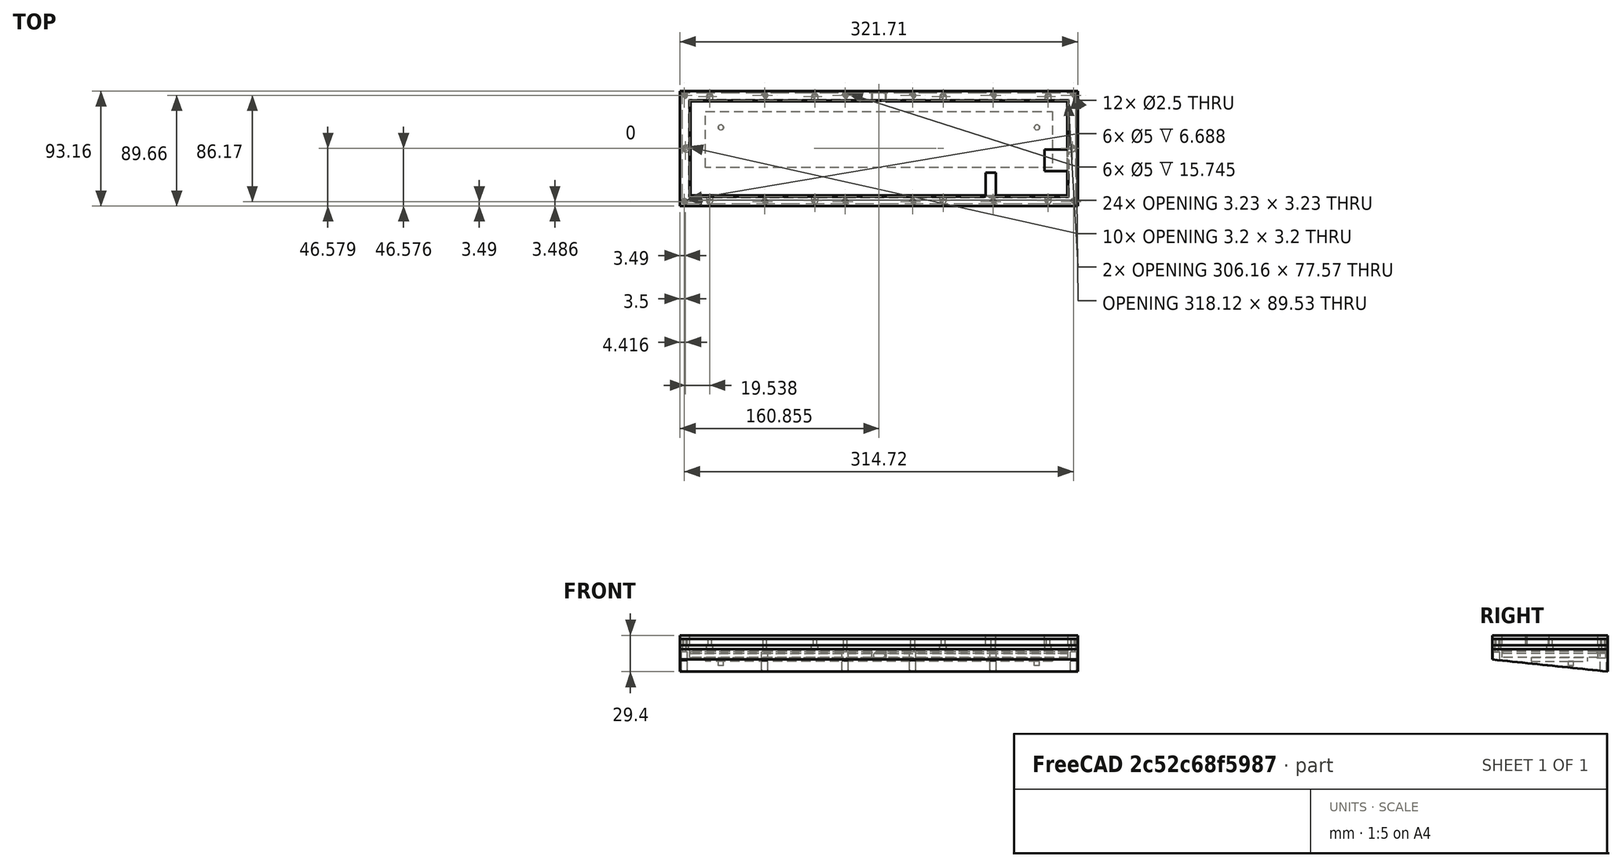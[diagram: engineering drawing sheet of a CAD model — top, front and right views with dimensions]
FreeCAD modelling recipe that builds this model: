
FCSTD DOCUMENT  (FreeCAD 0.19R24267 +99 (Git))
Label: chasma-case
License: All rights reserved
LicenseURL: http://en.wikipedia.org/wiki/All_rights_reserved
objects: Part::Feature×50, Part::MultiFuse×27, Part::Cylinder×24, Part::Extrusion×10, Part::Cut×4, Part::Compound×1
note: 116 computed .brp shape members not serialized (recipe doc carries the construction recipe); baked Part::Feature solids carry a one-line shape summary decoded from their .brp

FEATURE [Part::Feature] path7555
  shape: bbox 321.7 x 93.16 x 2e-07 mm, 0 faces, 0 solids (baked)
FEATURE [Part::Extrusion] Extrude
  Base = -> path7555
  Dir = (0,0,-1)
  DirMode = 0
  FaceMakerClass = Part::FaceMakerBullseye
  LengthFwd = 100
  LengthRev = 0
  Solid = true
  Symmetric = false
FEATURE [Part::Feature] path7555001
  Placement = pos=(-75,25,-14.03) rot=(-1,0,0;0.10472rad)
  shape: bbox 482.6 x 139 x 14.61 mm, 0 faces, 0 solids (baked)
FEATURE [Part::Extrusion] Extrude001
  Base = -> path7555001
  Dir = (0,-0.104528,-0.994522)
  DirMode = 2
  FaceMakerClass = Part::FaceMakerBullseye
  LengthFwd = 100
  LengthRev = 0
  Solid = true
  Symmetric = false
FEATURE [Part::Cut] Cut  label="bottom"
  Base = -> Extrude
  Tool = -> Extrude001
FEATURE [Part::Feature] path6345_8_6_9_7_6_0_4
  shape: bbox 306.2 x 77.57 x 2e-07 mm, 0 faces, 0 solids (baked)
FEATURE [Part::Feature] path6345_8_6_9_7_6_0_4001
  shape: bbox 321.7 x 93.16 x 2e-07 mm, 0 faces, 0 solids (baked)
FEATURE [Part::MultiFuse] Fusion
  Shapes = -> [path6345_8_6_9_7_6_0_4001,path6345_8_6_9_7_6_0_4]
FEATURE [Part::Extrusion] Extrude002  label="bottom-middle"
  Base = -> Fusion
  Dir = (0,0,1)
  DirMode = 2
  FaceMakerClass = Part::FaceMakerBullseye
  LengthFwd = 6.6
  LengthRev = 0
  Solid = true
  Symmetric = false
FEATURE [Part::MultiFuse] Fusion004  label="bottom-base"
  Shapes = -> [Cut,Extrude002]
FEATURE [Part::Cylinder] Cylinder  label="円柱"
  Angle = 360
  AttacherType = Attacher::AttachEngine3D
  Height = 30
  Placement = pos=(0,0,-18.6) rot=(0,0,1;0rad)
  Radius = 1.25
FEATURE [Part::Cylinder] Cylinder002  label="円柱001"
  Angle = 360
  AttacherType = Attacher::AttachEngine3D
  Height = 25
  Placement = pos=(0,0,-20.6) rot=(0,0,1;0rad)
  Radius = 2.5
FEATURE [Part::MultiFuse] Fusion006
  Placement = pos=(3.55,-3.55,0) rot=(0,0,1;0rad)
  Shapes = -> [Cylinder002,Cylinder]
FEATURE [Part::Cylinder] Cylinder003  label="円柱002"
  Angle = 360
  AttacherType = Attacher::AttachEngine3D
  Height = 25
  Placement = pos=(0,0,-20.6) rot=(0,0,1;0rad)
  Radius = 2.5
FEATURE [Part::Cylinder] Cylinder004  label="円柱003"
  Angle = 360
  AttacherType = Attacher::AttachEngine3D
  Height = 30
  Placement = pos=(0,0,-18.6) rot=(0,0,1;0rad)
  Radius = 1.25
FEATURE [Part::MultiFuse] Fusion007
  Placement = pos=(3.55,-89.72,0) rot=(0,0,1;0rad)
  Shapes = -> [Cylinder003,Cylinder004]
FEATURE [Part::MultiFuse] Fusion008
  Shapes = -> [Fusion006,Fusion007]
FEATURE [Part::Cylinder] Cylinder005  label="円柱004"
  Angle = 360
  AttacherType = Attacher::AttachEngine3D
  Height = 25
  Placement = pos=(0,0,-20.6) rot=(0,0,1;0rad)
  Radius = 2.5
FEATURE [Part::Cylinder] Cylinder006  label="円柱005"
  Angle = 360
  AttacherType = Attacher::AttachEngine3D
  Height = 25
  Placement = pos=(0,0,-20.6) rot=(0,0,1;0rad)
  Radius = 2.5
FEATURE [Part::Cylinder] Cylinder007  label="円柱006"
  Angle = 360
  AttacherType = Attacher::AttachEngine3D
  Height = 30
  Placement = pos=(0,0,-18.6) rot=(0,0,1;0rad)
  Radius = 1.25
FEATURE [Part::Cylinder] Cylinder008  label="円柱007"
  Angle = 360
  AttacherType = Attacher::AttachEngine3D
  Height = 30
  Placement = pos=(0,0,-18.6) rot=(0,0,1;0rad)
  Radius = 1.25
FEATURE [Part::MultiFuse] Fusion009
  Placement = pos=(3.55,-89.72,0) rot=(0,0,1;0rad)
  Shapes = -> [Cylinder006,Cylinder007]
FEATURE [Part::MultiFuse] Fusion011
  Placement = pos=(3.55,-3.55,0) rot=(0,0,1;0rad)
  Shapes = -> [Cylinder005,Cylinder008]
FEATURE [Part::MultiFuse] Fusion010
  Placement = pos=(130,0,0) rot=(0,0,1;0rad)
  Shapes = -> [Fusion011,Fusion009]
FEATURE [Part::Cylinder] Cylinder009  label="円柱008"
  Angle = 360
  AttacherType = Attacher::AttachEngine3D
  Height = 30
  Placement = pos=(0,0,-18.6) rot=(0,0,1;0rad)
  Radius = 1.25
FEATURE [Part::Cylinder] Cylinder010  label="円柱009"
  Angle = 360
  AttacherType = Attacher::AttachEngine3D
  Height = 25
  Placement = pos=(0,0,-20.6) rot=(0,0,1;0rad)
  Radius = 2.5
FEATURE [Part::Cylinder] Cylinder011  label="円柱010"
  Angle = 360
  AttacherType = Attacher::AttachEngine3D
  Height = 25
  Placement = pos=(0,0,-20.6) rot=(0,0,1;0rad)
  Radius = 2.5
FEATURE [Part::Cylinder] Cylinder012  label="円柱011"
  Angle = 360
  AttacherType = Attacher::AttachEngine3D
  Height = 30
  Placement = pos=(0,0,-18.6) rot=(0,0,1;0rad)
  Radius = 1.25
FEATURE [Part::MultiFuse] Fusion012
  Placement = pos=(3.55,-3.55,0) rot=(0,0,1;0rad)
  Shapes = -> [Cylinder010,Cylinder012]
FEATURE [Part::MultiFuse] Fusion013
  Placement = pos=(3.55,-89.72,0) rot=(0,0,1;0rad)
  Shapes = -> [Cylinder011,Cylinder009]
FEATURE [Part::MultiFuse] Fusion014
  Placement = pos=(65,0,0) rot=(0,0,1;0rad)
  Shapes = -> [Fusion012,Fusion013]
FEATURE [Part::Cylinder] Cylinder013  label="円柱012"
  Angle = 360
  AttacherType = Attacher::AttachEngine3D
  Height = 30
  Placement = pos=(0,0,-18.6) rot=(0,0,1;0rad)
  Radius = 1.25
FEATURE [Part::Cylinder] Cylinder014  label="円柱013"
  Angle = 360
  AttacherType = Attacher::AttachEngine3D
  Height = 30
  Placement = pos=(0,0,-18.6) rot=(0,0,1;0rad)
  Radius = 1.25
FEATURE [Part::Cylinder] Cylinder015  label="円柱014"
  Angle = 360
  AttacherType = Attacher::AttachEngine3D
  Height = 25
  Placement = pos=(0,0,-20.6) rot=(0,0,1;0rad)
  Radius = 2.5
FEATURE [Part::Cylinder] Cylinder016  label="円柱015"
  Angle = 360
  AttacherType = Attacher::AttachEngine3D
  Height = 25
  Placement = pos=(0,0,-20.6) rot=(0,0,1;0rad)
  Radius = 2.5
FEATURE [Part::MultiFuse] Fusion015
  Placement = pos=(3.55,-3.55,0) rot=(0,0,1;0rad)
  Shapes = -> [Cylinder015,Cylinder014]
FEATURE [Part::MultiFuse] Fusion016
  Placement = pos=(3.55,-89.72,0) rot=(0,0,1;0rad)
  Shapes = -> [Cylinder016,Cylinder013]
FEATURE [Part::MultiFuse] Fusion017
  Placement = pos=(184.72,0,0) rot=(0,0,1;0rad)
  Shapes = -> [Fusion015,Fusion016]
FEATURE [Part::Cylinder] Cylinder017  label="円柱016"
  Angle = 360
  AttacherType = Attacher::AttachEngine3D
  Height = 30
  Placement = pos=(0,0,-18.6) rot=(0,0,1;0rad)
  Radius = 1.25
FEATURE [Part::Cylinder] Cylinder018  label="円柱017"
  Angle = 360
  AttacherType = Attacher::AttachEngine3D
  Height = 30
  Placement = pos=(0,0,-18.6) rot=(0,0,1;0rad)
  Radius = 1.25
FEATURE [Part::Cylinder] Cylinder019  label="円柱018"
  Angle = 360
  AttacherType = Attacher::AttachEngine3D
  Height = 25
  Placement = pos=(0,0,-20.6) rot=(0,0,1;0rad)
  Radius = 2.5
FEATURE [Part::Cylinder] Cylinder020  label="円柱019"
  Angle = 360
  AttacherType = Attacher::AttachEngine3D
  Height = 25
  Placement = pos=(0,0,-20.6) rot=(0,0,1;0rad)
  Radius = 2.5
FEATURE [Part::MultiFuse] Fusion018
  Placement = pos=(3.55,-89.72,0) rot=(0,0,1;0rad)
  Shapes = -> [Cylinder020,Cylinder017]
FEATURE [Part::MultiFuse] Fusion019
  Placement = pos=(3.55,-3.55,0) rot=(0,0,1;0rad)
  Shapes = -> [Cylinder019,Cylinder018]
FEATURE [Part::MultiFuse] Fusion020
  Placement = pos=(249.72,0,0) rot=(0,0,1;0rad)
  Shapes = -> [Fusion019,Fusion018]
FEATURE [Part::Cylinder] Cylinder021  label="円柱020"
  Angle = 360
  AttacherType = Attacher::AttachEngine3D
  Height = 25
  Placement = pos=(0,0,-20.6) rot=(0,0,1;0rad)
  Radius = 2.5
FEATURE [Part::Cylinder] Cylinder022  label="円柱021"
  Angle = 360
  AttacherType = Attacher::AttachEngine3D
  Height = 30
  Placement = pos=(0,0,-18.6) rot=(0,0,1;0rad)
  Radius = 1.25
FEATURE [Part::Cylinder] Cylinder023  label="円柱022"
  Angle = 360
  AttacherType = Attacher::AttachEngine3D
  Height = 30
  Placement = pos=(0,0,-18.6) rot=(0,0,1;0rad)
  Radius = 1.25
FEATURE [Part::Cylinder] Cylinder024  label="円柱023"
  Angle = 360
  AttacherType = Attacher::AttachEngine3D
  Height = 25
  Placement = pos=(0,0,-20.6) rot=(0,0,1;0rad)
  Radius = 2.5
FEATURE [Part::MultiFuse] Fusion021
  Placement = pos=(3.55,-3.55,0) rot=(0,0,1;0rad)
  Shapes = -> [Cylinder024,Cylinder023]
FEATURE [Part::MultiFuse] Fusion022
  Placement = pos=(3.55,-89.72,0) rot=(0,0,1;0rad)
  Shapes = -> [Cylinder021,Cylinder022]
FEATURE [Part::MultiFuse] Fusion023
  Placement = pos=(314.72,0,0) rot=(0,0,1;0rad)
  Shapes = -> [Fusion021,Fusion022]
FEATURE [Part::MultiFuse] Fusion024
  Shapes = -> [Fusion008,Fusion010,Fusion014,Fusion017,Fusion020,Fusion023]
FEATURE [Part::Cut] Cut001  label="bottom-screw"
  Base = -> Fusion004
  Tool = -> Fusion024
FEATURE [Part::Feature] path10122_7
  shape: bbox 304.8 x 83.09 x 2e-07 mm, 1 faces, 0 solids (baked)
FEATURE [Part::Extrusion] Extrude006  label="pcb"
  Base = -> path10122_7
  Dir = (0,0,1)
  DirMode = 0
  FaceMakerClass = Part::FaceMakerBullseye
  LengthFwd = 1.6
  LengthRev = 0
  Placement = pos=(0,0,3.4) rot=(0,0,1;0rad)
  Solid = false
  Symmetric = false
FEATURE [Part::Feature] rect340
  shape: bbox 11.23 x 6.92 x 2e-07 mm, 0 faces, 0 solids (baked)
FEATURE [Part::Extrusion] Extrude007  label="usb-box"
  Base = -> rect340
  Dir = (0,0,1)
  DirMode = 0
  FaceMakerClass = Part::FaceMakerBullseye
  LengthFwd = 10
  LengthRev = 0
  Placement = pos=(0,0,-0.5) rot=(0,0,1;0rad)
  Solid = true
  Symmetric = false
FEATURE [Part::Feature] hull004  label="usb-hole-base"
  Placement = pos=(-154.9,0,-0.8) rot=(0,0,1;0rad)
  shape: bbox 9.26 x 10 x 3.733 mm, 28 faces (baked)
FEATURE [Part::MultiFuse] Fusion027  label="usb-hole"
  Shapes = -> [hull004,Extrude007]
FEATURE [Part::Cut] Cut002  label="bottom-usb"
  Base = -> Cut001
  Tool = -> Fusion027
FEATURE [Part::Feature] rect666
  shape: bbox 280.5 x 45.5 x 2e-07 mm, 0 faces, 0 solids (baked)
FEATURE [Part::Extrusion] Extrude008
  Base = -> rect666
  Dir = (0,0,-1)
  DirMode = 0
  FaceMakerClass = Part::FaceMakerBullseye
  LengthFwd = 3.2
  LengthRev = 0
  Solid = true
  Symmetric = false
FEATURE [Part::Feature] circle686
  Placement = pos=(33.055,-34.6382,0) rot=(0,0,1;0rad)
  shape: bbox 4.675 x 5.113 x 2e-07 mm, 0 faces, 0 solids (baked)
FEATURE [Part::Feature] circle690
  Placement = pos=(288.755,-34.6377,0) rot=(0,0,1;0rad)
  shape: bbox 4.675 x 5.113 x 2e-07 mm, 0 faces, 0 solids (baked)
FEATURE [Part::MultiFuse] Fusion028
  Shapes = -> [circle690,circle686]
FEATURE [Part::Extrusion] Extrude009
  Base = -> Fusion028
  Dir = (0,0,1)
  DirMode = 2
  FaceMakerClass = Part::FaceMakerBullseye
  LengthFwd = 0
  LengthRev = 6.5
  Solid = true
  Symmetric = false
FEATURE [Part::MultiFuse] Fusion029
  Shapes = -> [Extrude009,Extrude008]
FEATURE [Part::Cut] Cut003  label="bottom-case"
  Base = -> Cut002
  Tool = -> Fusion029
FEATURE [Part::Feature] path6345_8_6_9_7_6_0_8_7_8_2
  shape: bbox 321.7 x 93.16 x 2e-07 mm, 0 faces, 0 solids (baked)
FEATURE [Part::Feature] path6345_8_6_9_7_6_0_8_7_8_2001
  shape: bbox 318.1 x 89.53 x 2e-07 mm, 0 faces, 0 solids (baked)
FEATURE [Part::Feature] path1723_2_4
  Placement = pos=(3.54,-3.54,0) rot=(0,0,1;0rad)
  shape: bbox 3.566 x 3.899 x 2e-07 mm, 0 faces, 0 solids (baked)
FEATURE [Part::Feature] path1723_2_4_9_4
  Placement = pos=(3.54,-89.724,0) rot=(0,0,1;0rad)
  shape: bbox 3.566 x 3.899 x 2e-07 mm, 0 faces, 0 solids (baked)
FEATURE [Part::Feature] path1723_2_4_9_2
  Placement = pos=(68.54,-3.54,0) rot=(0,0,1;0rad)
  shape: bbox 3.566 x 3.899 x 2e-07 mm, 0 faces, 0 solids (baked)
FEATURE [Part::Feature] path1723_2_4_9_4_5
  Placement = pos=(68.54,-89.724,0) rot=(0,0,1;0rad)
  shape: bbox 3.566 x 3.899 x 2e-07 mm, 0 faces, 0 solids (baked)
FEATURE [Part::Feature] path1723_2_4_9_2_7
  Placement = pos=(133.54,-3.54,0) rot=(0,0,1;0rad)
  shape: bbox 3.566 x 3.899 x 2e-07 mm, 0 faces, 0 solids (baked)
FEATURE [Part::Feature] path1723_2_4_9_4_5_7
  Placement = pos=(133.54,-89.724,0) rot=(0,0,1;0rad)
  shape: bbox 3.566 x 3.899 x 2e-07 mm, 0 faces, 0 solids (baked)
FEATURE [Part::Feature] path1723_2_4_3
  Placement = pos=(-318.269,-3.54,0) rot=(0,0,1;0rad)
  shape: bbox 3.566 x 3.899 x 2e-07 mm, 0 faces, 0 solids (baked)
FEATURE [Part::Feature] path1723_2_4_9_4_4
  Placement = pos=(-318.269,-89.724,0) rot=(0,0,1;0rad)
  shape: bbox 3.566 x 3.899 x 2e-07 mm, 0 faces, 0 solids (baked)
FEATURE [Part::Feature] path1723_2_4_9_2_5
  Placement = pos=(-253.269,-3.54,0) rot=(0,0,1;0rad)
  shape: bbox 3.566 x 3.899 x 2e-07 mm, 0 faces, 0 solids (baked)
FEATURE [Part::Feature] path1723_2_4_9_4_5_8
  Placement = pos=(-253.269,-89.724,0) rot=(0,0,1;0rad)
  shape: bbox 3.566 x 3.899 x 2e-07 mm, 0 faces, 0 solids (baked)
FEATURE [Part::Feature] path1723_2_4_9_2_7_8
  Placement = pos=(-188.269,-3.54,0) rot=(0,0,1;0rad)
  shape: bbox 3.566 x 3.899 x 2e-07 mm, 0 faces, 0 solids (baked)
FEATURE [Part::Feature] path1723_2_4_9_4_5_7_3
  Placement = pos=(-188.269,-89.724,0) rot=(0,0,1;0rad)
  shape: bbox 3.566 x 3.899 x 2e-07 mm, 0 faces, 0 solids (baked)
FEATURE [Part::MultiFuse] Fusion030
  Shapes = -> [path6345_8_6_9_7_6_0_8_7_8_2,path6345_8_6_9_7_6_0_8_7_8_2001,path1723_2_4,path1723_2_4_9_4,path1723_2_4_9_2,path1723_2_4_9_4_5,path1723_2_4_9_2_7,path1723_2_4_9_4_5_7,path1723_2_4_3,path1723_2_4_9_4_4,path1723_2_4_9_2_5,path1723_2_4_9_4_5_8,path1723_2_4_9_2_7_8,path1723_2_4_9_4_5_7_3]
FEATURE [Part::Extrusion] Extrude010  label="top-middle"
  Base = -> Fusion030
  Dir = (0,0,1)
  DirMode = 2
  FaceMakerClass = Part::FaceMakerBullseye
  LengthFwd = 3.4
  LengthRev = 0
  Placement = pos=(0,0,6.6) rot=(0,0,1;0rad)
  Solid = true
  Symmetric = false
FEATURE [Part::Feature] path2905
  Placement = pos=(24.004,-4.48756,0) rot=(0,0,1;0rad)
  shape: bbox 3.536 x 3.867 x 2e-07 mm, 0 faces, 0 solids (baked)
FEATURE [Part::Feature] path2905_3
  Placement = pos=(109.004,-4.48756,0) rot=(0,0,1;0rad)
  shape: bbox 3.536 x 3.867 x 2e-07 mm, 0 faces, 0 solids (baked)
FEATURE [Part::Feature] path2905_0
  Placement = pos=(212.805,-4.48756,0) rot=(0,0,1;0rad)
  shape: bbox 3.536 x 3.867 x 2e-07 mm, 0 faces, 0 solids (baked)
FEATURE [Part::Feature] path2905_5
  Placement = pos=(297.805,-4.48756,0) rot=(0,0,1;0rad)
  shape: bbox 3.536 x 3.867 x 2e-07 mm, 0 faces, 0 solids (baked)
FEATURE [Part::Feature] path2905_1
  Placement = pos=(317.345,-46.6329,0) rot=(0,0,1;0rad)
  shape: bbox 3.536 x 3.867 x 2e-07 mm, 0 faces, 0 solids (baked)
FEATURE [Part::Feature] path2905_7
  Placement = pos=(297.805,-88.7792,0) rot=(0,0,1;0rad)
  shape: bbox 3.536 x 3.867 x 2e-07 mm, 0 faces, 0 solids (baked)
FEATURE [Part::Feature] path2905_01
  Placement = pos=(212.805,-88.7792,0) rot=(0,0,1;0rad)
  shape: bbox 3.536 x 3.867 x 2e-07 mm, 0 faces, 0 solids (baked)
FEATURE [Part::Feature] path2905_8
  Placement = pos=(109.004,-88.7792,0) rot=(0,0,1;0rad)
  shape: bbox 3.536 x 3.867 x 2e-07 mm, 0 faces, 0 solids (baked)
FEATURE [Part::Feature] path2905_2
  Placement = pos=(24.004,-88.7792,0) rot=(0,0,1;0rad)
  shape: bbox 3.536 x 3.867 x 2e-07 mm, 0 faces, 0 solids (baked)
FEATURE [Part::Feature] path2905_11
  Placement = pos=(4.4662,-46.6342,0) rot=(0,0,1;0rad)
  shape: bbox 3.536 x 3.867 x 2e-07 mm, 0 faces, 0 solids (baked)
FEATURE [Part::Feature] path1723_2_4_0
  Placement = pos=(3.54,-3.54,0) rot=(0,0,1;0rad)
  shape: bbox 3.566 x 3.899 x 2e-07 mm, 0 faces, 0 solids (baked)
FEATURE [Part::Feature] path1723_2_4_9_4_2
  Placement = pos=(3.54,-89.724,0) rot=(0,0,1;0rad)
  shape: bbox 3.566 x 3.899 x 2e-07 mm, 0 faces, 0 solids (baked)
FEATURE [Part::Feature] path1723_2_4_9_2_0
  Placement = pos=(68.54,-3.54,0) rot=(0,0,1;0rad)
  shape: bbox 3.566 x 3.899 x 2e-07 mm, 0 faces, 0 solids (baked)
FEATURE [Part::Feature] path1723_2_4_9_4_5_4
  Placement = pos=(68.54,-89.724,0) rot=(0,0,1;0rad)
  shape: bbox 3.566 x 3.899 x 2e-07 mm, 0 faces, 0 solids (baked)
FEATURE [Part::Feature] path1723_2_4_9_2_7_1
  Placement = pos=(133.54,-3.54,0) rot=(0,0,1;0rad)
  shape: bbox 3.566 x 3.899 x 2e-07 mm, 0 faces, 0 solids (baked)
FEATURE [Part::Feature] path1723_2_4_9_4_5_7_39
  Placement = pos=(133.54,-89.724,0) rot=(0,0,1;0rad)
  shape: bbox 3.566 x 3.899 x 2e-07 mm, 0 faces, 0 solids (baked)
FEATURE [Part::Feature] path1723_2_4_3_6
  Placement = pos=(-318.269,-3.54,0) rot=(0,0,1;0rad)
  shape: bbox 3.566 x 3.899 x 2e-07 mm, 0 faces, 0 solids (baked)
FEATURE [Part::Feature] path1723_2_4_9_4_4_8
  Placement = pos=(-318.269,-89.724,0) rot=(0,0,1;0rad)
  shape: bbox 3.566 x 3.899 x 2e-07 mm, 0 faces, 0 solids (baked)
FEATURE [Part::Feature] path1723_2_4_9_2_5_7
  Placement = pos=(-253.269,-3.54,0) rot=(0,0,1;0rad)
  shape: bbox 3.566 x 3.899 x 2e-07 mm, 0 faces, 0 solids (baked)
FEATURE [Part::Feature] path1723_2_4_9_4_5_8_1
  Placement = pos=(-253.269,-89.724,0) rot=(0,0,1;0rad)
  shape: bbox 3.566 x 3.899 x 2e-07 mm, 0 faces, 0 solids (baked)
FEATURE [Part::Feature] path1723_2_4_9_2_7_8_7
  Placement = pos=(-188.269,-3.54,0) rot=(0,0,1;0rad)
  shape: bbox 3.566 x 3.899 x 2e-07 mm, 0 faces, 0 solids (baked)
FEATURE [Part::Feature] path1723_2_4_9_4_5_7_3_4
  Placement = pos=(-188.269,-89.724,0) rot=(0,0,1;0rad)
  shape: bbox 3.566 x 3.899 x 2e-07 mm, 0 faces, 0 solids (baked)
FEATURE [Part::Feature] path24134
  shape: bbox 306.2 x 77.57 x 2e-07 mm, 0 faces, 0 solids (baked)
FEATURE [Part::Feature] path24134001
  shape: bbox 321.7 x 93.16 x 2e-07 mm, 0 faces, 0 solids (baked)
FEATURE [Part::MultiFuse] Fusion031
  Shapes = -> [path2905,path2905_3,path2905_0,path2905_5,path2905_1,path2905_7,path2905_01,path2905_8,path2905_2,path2905_11,path1723_2_4_0,path1723_2_4_9_4_2,path1723_2_4_9_2_0,path1723_2_4_9_4_5_4,path1723_2_4_9_2_7_1,path1723_2_4_9_4_5_7_39,path1723_2_4_3_6,path1723_2_4_9_4_4_8,path1723_2_4_9_2_5_7,path1723_2_4_9_4_5_8_1,path1723_2_4_9_2_7_8_7,path1723_2_4_9_4_5_7_3_4,path24134,path24134001]
FEATURE [Part::Extrusion] Extrude011  label="top-insert"
  Base = -> Fusion031
  Dir = (0,0,1)
  DirMode = 2
  FaceMakerClass = Part::FaceMakerBullseye
  LengthFwd = 5
  LengthRev = 0
  Placement = pos=(0,0,10) rot=(0,0,1;0rad)
  Solid = true
  Symmetric = false
FEATURE [Part::Feature] rect88279
  shape: bbox 321.7 x 93.16 x 2e-07 mm, 0 faces, 0 solids (baked)
FEATURE [Part::Feature] path24134_3
  shape: bbox 306.2 x 77.57 x 2e-07 mm, 0 faces, 0 solids (baked)
FEATURE [Part::MultiFuse] Fusion032
  Placement = pos=(0,0,15) rot=(0,0,1;0rad)
  Shapes = -> [rect88279,path24134_3]
FEATURE [Part::Extrusion] Extrude012  label="top"
  Base = -> Fusion032
  Dir = (0,0,1)
  DirMode = 2
  FaceMakerClass = Part::FaceMakerBullseye
  LengthFwd = 3
  LengthRev = 0
  Solid = true
  Symmetric = false
FEATURE [Part::Compound] Compound  label="top-case"
  Links = -> [Extrude012,Extrude011,Extrude010]
